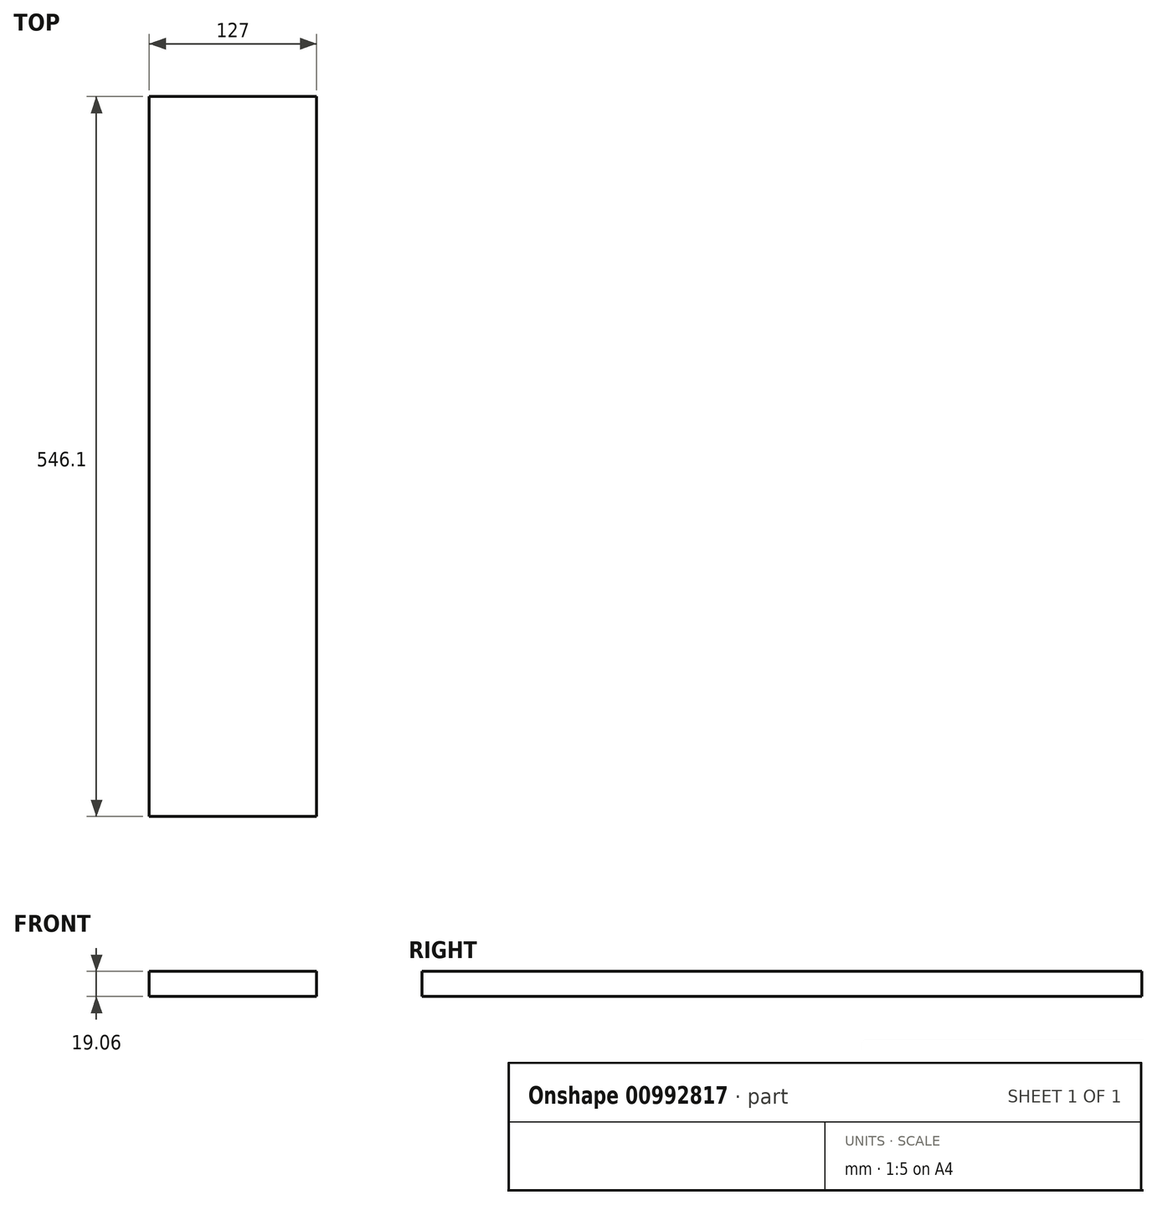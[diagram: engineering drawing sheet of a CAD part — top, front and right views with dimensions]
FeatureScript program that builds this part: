
annotation { "Feature Type Name" : "Feature", "Feature Type Description" : "" }
export const myFeature = defineFeature(function(context is Context, id is Id, definition is map)
    precondition{}
    {
        {
            var Q0;
            Q0=qCreatedBy(makeId("Front.planeOp"),FACE);
            var sketch = newSketch(context, id + "F0", { "sketchPlane" : qUnion([Q0])});
            skLineSegment(sketch, "E0", {"start": v(0, 9.52) * mm, "end": v(0, -9.53) * mm, "construction": true});
            skLineSegment(sketch, "E1", {"start": v(63.5, 0) * mm, "end": v(-63.5, 0) * mm, "construction": true});
            skLineSegment(sketch, "E2.bottom", {"start": v(63.5, -9.53) * mm, "end": v(-63.5, -9.53) * mm});
            skLineSegment(sketch, "E2.top", {"start": v(63.5, 9.53) * mm, "end": v(-63.5, 9.53) * mm});
            skLineSegment(sketch, "E2.left", {"start": v(63.5, -9.53) * mm, "end": v(63.5, 9.53) * mm});
            skLineSegment(sketch, "E2.right", {"start": v(-63.5, -9.53) * mm, "end": v(-63.5, 9.53) * mm});
            skPoint(sketch, "E2.middle", {"position": v(0, 0) * mm});
            skSolve(sketch);
        }
        {
            var Q0;
            Q0=qSketchRegion(id+"F0",true);
            extrude(context, id + "F1", {"entities" : qUnion([Q0]), "endBound" : BoundingType.SYMMETRIC, "depth" : 546.1 * mm, "offsetDistance" : 25.4 * mm});
        }
    });
